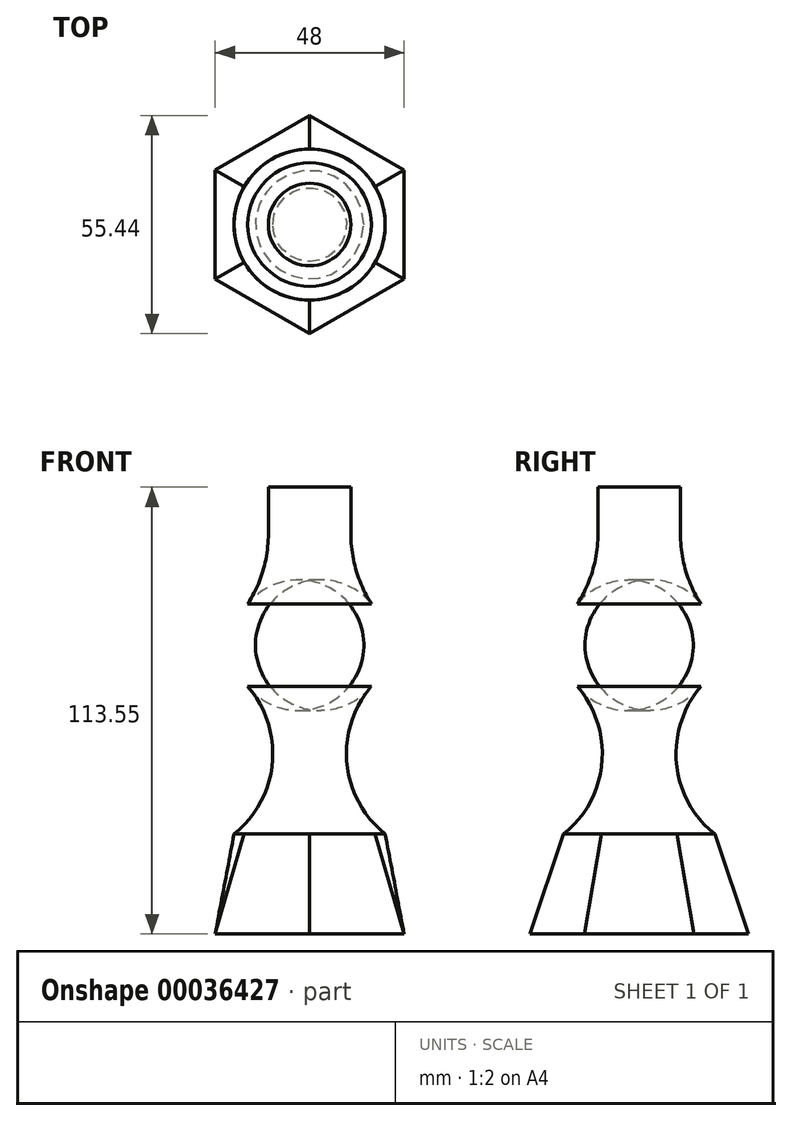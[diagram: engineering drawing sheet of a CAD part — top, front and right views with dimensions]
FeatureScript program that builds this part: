
annotation { "Feature Type Name" : "Feature", "Feature Type Description" : "" }
export const myFeature = defineFeature(function(context is Context, id is Id, definition is map)
    precondition{}
    {
        {
            var Q0;
            Q0=qCreatedBy(makeId("Front.planeOp"),FACE);
            var sketch = newSketch(context, id + "F0", { "sketchPlane" : qUnion([Q0])});
            skLineSegment(sketch, "E0", {"start": v(-19.2, -30.98) * mm, "end": v(0, -30.98) * mm});
            skLineSegment(sketch, "E1", {"start": v(0, -30.98) * mm, "end": v(0, 57.17) * mm});
            skLineSegment(sketch, "E2", {"start": v(0, 57.17) * mm, "end": v(-10.47, 57.17) * mm});
            skLineSegment(sketch, "E3", {"start": v(-10.47, 57.17) * mm, "end": v(-10.47, 45.39) * mm});
            skArc(sketch, "E4", {"start": v(-15.71, 27.5) * mm, "mid": v(-11.8, 36.06) * mm, "end": v(-10.47, 45.39) * mm});
            skArc(sketch, "E5", {"start": v(-15.71, 27.5) * mm, "mid": v(-19.43, 17.02) * mm, "end": v(-15.71, 6.55) * mm});
            skArc(sketch, "E6", {"start": v(-19.2, -30.98) * mm, "mid": v(-9.47, -12.96) * mm, "end": v(-15.71, 6.55) * mm});
            skSolve(sketch);
        }
        {
            var Q0;
            Q0=makeQuery(id+"F0.imprint","IMPRINT",FACE,{"disambiguationData":[TD([[makeQuery(id+"F0.imprint","IMPRINT",EDGE,{"derivedFrom":sQuery(id+"F0.wireOp",EDGE,"E0")}),1.0]])]});
            var Q1;
            Q1=sQuery(id+"F0.wireOp",EDGE,"E1");
            revolve(context, id + "F1", {"entities" : qUnion([Q0]), "axis" : qUnion([Q1]), "revolveType" : RevolveType.FULL});
        }
        {
            var Q0;
            Q0=makeQuery(id+"F1.opRevolve","SWEPT_FACE",FACE,{"disambiguationData":[OSD([sQuery(id+"F0.wireOp",EDGE,"E0")])]});
            cPlane(context, id + "F2", {"entities" : qUnion([Q0]), "cplaneType" : CPlaneType.OFFSET, "offset" : 25.4 * mm, "width" : 152.4 * mm, "height" : 152.4 * mm});
        }
        {
            var Q0;
            Q0=qCreatedBy(id+"F2.planeOp",FACE);
            var sketch = newSketch(context, id + "F3", { "sketchPlane" : qUnion([Q0])});
            skCircle(sketch, "E7.cCircle", {"center": v(0, 0) * mm, "radius": 24 * mm, "construction": true});
            skLineSegment(sketch, "E7.0", {"start": v(-24, -13.86) * mm, "end": v(-24, 13.86) * mm});
            skLineSegment(sketch, "E7.1", {"start": v(-24, 13.86) * mm, "end": v(0, 27.72) * mm});
            skLineSegment(sketch, "E7.2", {"start": v(0, 27.72) * mm, "end": v(24, 13.86) * mm});
            skLineSegment(sketch, "E7.3", {"start": v(24, 13.86) * mm, "end": v(24, -13.86) * mm});
            skLineSegment(sketch, "E7.4", {"start": v(24, -13.86) * mm, "end": v(0, -27.72) * mm});
            skLineSegment(sketch, "E7.5", {"start": v(0, -27.72) * mm, "end": v(-24, -13.86) * mm});
            skPoint(sketch, "E7.0.midPoint", {"position": v(-24, 0) * mm});
            skSolve(sketch);
        }
        {
            var Q0;
            Q0=makeQuery(id+"F1.opRevolve","SWEPT_FACE",FACE,{"disambiguationData":[OSD([sQuery(id+"F0.wireOp",EDGE,"E0")])]});
            var Q1;
            Q1=makeQuery(id+"F3.imprint","IMPRINT",FACE,{"disambiguationData":[TD([[makeQuery(id+"F3.imprint","IMPRINT",EDGE,{"derivedFrom":sQuery(id+"F3.wireOp",EDGE,"E7.0")}),-1.0]])]});
            loft(context, id + "F4", {"sheetProfilesArray" : [{ "sheetProfileEntities" : qUnion([Q0]) }, { "sheetProfileEntities" : qUnion([Q1]) }]});
        }
    });
